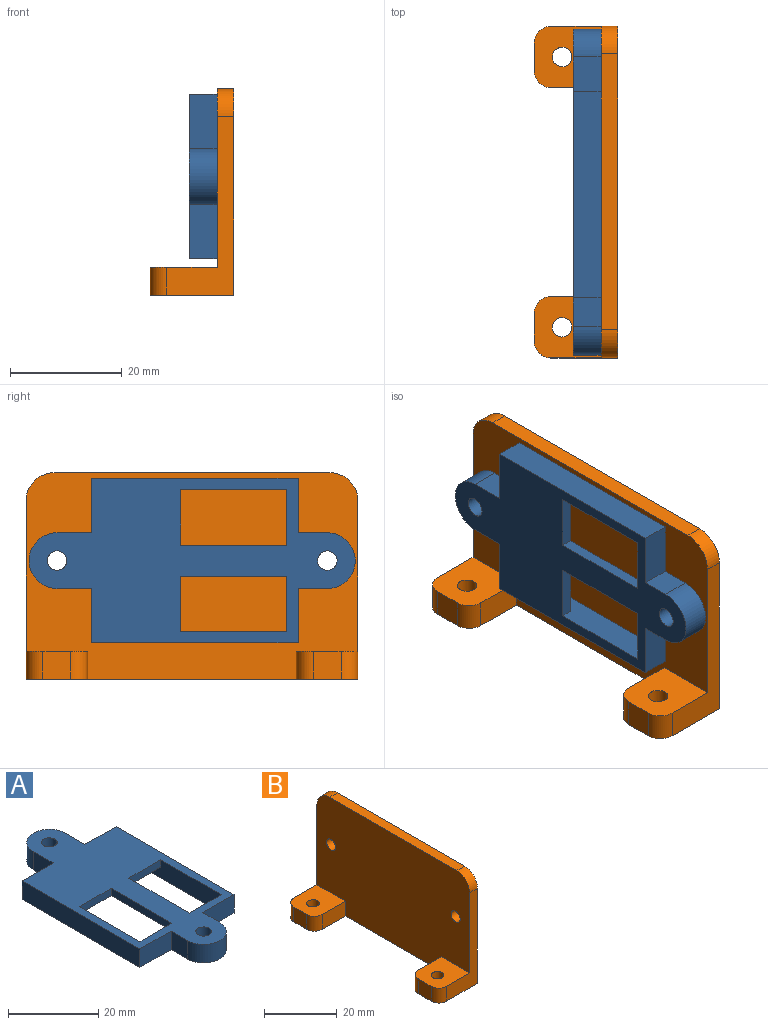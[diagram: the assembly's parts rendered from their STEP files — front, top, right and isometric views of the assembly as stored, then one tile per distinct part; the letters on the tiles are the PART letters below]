
ASSEMBLY  parts=2 mates=1
PART A: 25 faces, bbox 29.5x58.4x5 mm
  f0: plane 58.43x29.5mm, normal (0,0,1), area 885.1mm2, adj f2,f3,f4,f5,f6,f7,f8,f9
  f1: plane 58.43x29.5mm, normal (0,0,-1), area 423.6mm2, adj f2,f3,f4,f5,f6,f7,f8,f9
  f2: plane 9.75x5mm, normal (0,1,0), area 48.8mm2, adj f0,f1,f3,f14
  f3: plane 6.18x5mm, normal (1,0,0), area 30.9mm2, adj f0,f1,f2,f4
  f4: cylinder r=5mm len=10mm, axis (0,0,-1), area 78.5mm2, adj f0,f1,f3,f5
  f5: plane 6.18x5mm, normal (-1,0,0), area 30.9mm2, adj f0,f1,f4,f6
  f6: plane 9.75x5mm, normal (0,1,0), area 48.7mm2, adj f0,f1,f5,f7
  f7: plane 37x5mm, normal (-1,0,0), area 185mm2, adj f0,f1,f6,f8
  f8: plane 9.75x5mm, normal (0,-1,0), area 48.7mm2, adj f0,f1,f7,f9
  f9: plane 5.24x5mm, normal (-1,0,0), area 26.2mm2, adj f0,f1,f8,f10
  f10: cylinder r=5mm len=10mm, axis (0,0,-1), area 79.4mm2, adj f0,f1,f9,f11
  f11: plane 5.07x5mm, normal (1,0,0), area 25.4mm2, adj f0,f1,f10,f12
  f12: plane 9.75x5mm, normal (0,-1,0), area 48.8mm2, adj f0,f1,f11,f14
  f13: cylinder r=1.75mm len=5mm, axis (0,0,-1), area 55mm2, adj f0,f1
  f14: plane 37x5mm, normal (1,0,0), area 185mm2, adj f0,f1,f2,f12
  f15: cylinder r=1.75mm len=5mm, axis (0,0,-1), area 55mm2, adj f0,f1
  f16: plane 19x2mm, normal (1,0,0), area 38mm2, adj f0,f17,f19,f20
  f17: plane 25.5x5mm, normal (0,1,0), area 116.5mm2, adj f0,f1,f16,f18,f20,f21,f22
  f18: plane 33x5mm, normal (-1,0,0), area 137mm2, adj f0,f1,f17,f19,f20,f24
  f19: plane 10x2mm, normal (0,-1,0), area 20mm2, adj f0,f16,f18,f20
  f20: plane 33x25.5mm, normal (0,0,-1), area 461.5mm2, adj f16,f17,f18,f19,f21,f22,f23,f24
  f21: plane 33x5mm, normal (1,0,0), area 137mm2, adj f0,f1,f17,f20,f23,f24
  f22: plane 19x2mm, normal (-1,0,0), area 38mm2, adj f0,f17,f20,f23
  f23: plane 10x2mm, normal (0,-1,0), area 20mm2, adj f0,f20,f21,f22
  f24: plane 25.5x3mm, normal (0,-1,0), area 76.5mm2, adj f1,f18,f20,f21
PART B: 22 faces, bbox 15x59.4x37 mm
  f0: plane 12x11mm, normal (0,0,1), area 118.5mm2, adj f7,f8,f9,f10,f11,f12,f13
  f1: plane 12x11mm, normal (0,0,1), area 118.5mm2, adj f2,f3,f4,f5,f6,f7,f15
  f2: plane 32x12mm, normal (0,1,0), area 141mm2, adj f1,f3,f7,f14,f16,f18
  f3: cylinder r=3mm len=5mm, axis (0,0,-1), area 23.6mm2, adj f1,f2,f4,f16
  f4: plane 5x5mm, normal (-1,0,0), area 25mm2, adj f1,f3,f5,f16
  f5: cylinder r=3mm len=5mm, axis (0,0,-1), area 23.6mm2, adj f1,f4,f6,f16
  f6: plane 9x5mm, normal (0,-1,0), area 45mm2, adj f1,f5,f7,f16
  f7: plane 59.42x37mm, normal (-1,0,0), area 2058.7mm2, adj f0,f1,f2,f6,f8,f12,f16,f17
  f8: plane 9x5mm, normal (0,1,0), area 45mm2, adj f0,f7,f9,f16
  f9: cylinder r=3mm len=5mm, axis (0,0,-1), area 23.6mm2, adj f0,f8,f10,f16
  f10: plane 5x5mm, normal (-1,0,0), area 25mm2, adj f0,f9,f11,f16
  f11: cylinder r=3mm len=5mm, axis (0,0,-1), area 23.6mm2, adj f0,f10,f12,f16
  f12: plane 32x12mm, normal (0,-1,0), area 141mm2, adj f0,f7,f11,f14,f16,f19
  f13: cylinder r=1.75mm len=5mm, axis (0,0,-1), area 55mm2, adj f0,f16
  f14: plane 59.42x37mm, normal (1,0,0), area 2168.7mm2, adj f2,f12,f16,f17,f18,f19,f20,f21
  f15: cylinder r=1.75mm len=5mm, axis (0,0,-1), area 55mm2, adj f1,f16
  f16: plane 59.42x15mm, normal (0,0,-1), area 415.3mm2, adj f2,f3,f4,f5,f6,f7,f8,f9
  f17: plane 49.42x3mm, normal (0,0,1), area 148.3mm2, adj f7,f14,f18,f19
  f18: cylinder r=5mm len=5mm, axis (1,0,0), area 23.6mm2, adj f2,f7,f14,f17
  f19: cylinder r=5mm len=5mm, axis (-1,0,0), area 23.6mm2, adj f7,f12,f14,f17
  f20: cylinder r=1.75mm len=3.5mm, axis (-1,0,0), area 33mm2, adj f7,f14
  f21: cylinder r=1.75mm len=3.5mm, axis (-1,0,0), area 33mm2, adj f7,f14
PLACE A rot(axis=(0,-1,0),90deg) t=(-10.32,2.12,43.16)mm
PLACE B rot(axis=(-1,0,0),0deg) t=(6.97,4.04,2.37)mm
MATE parallel A.f14 <-> B.f17  axis (0,0,1) through (-10.32,-5.8,38.37)mm
